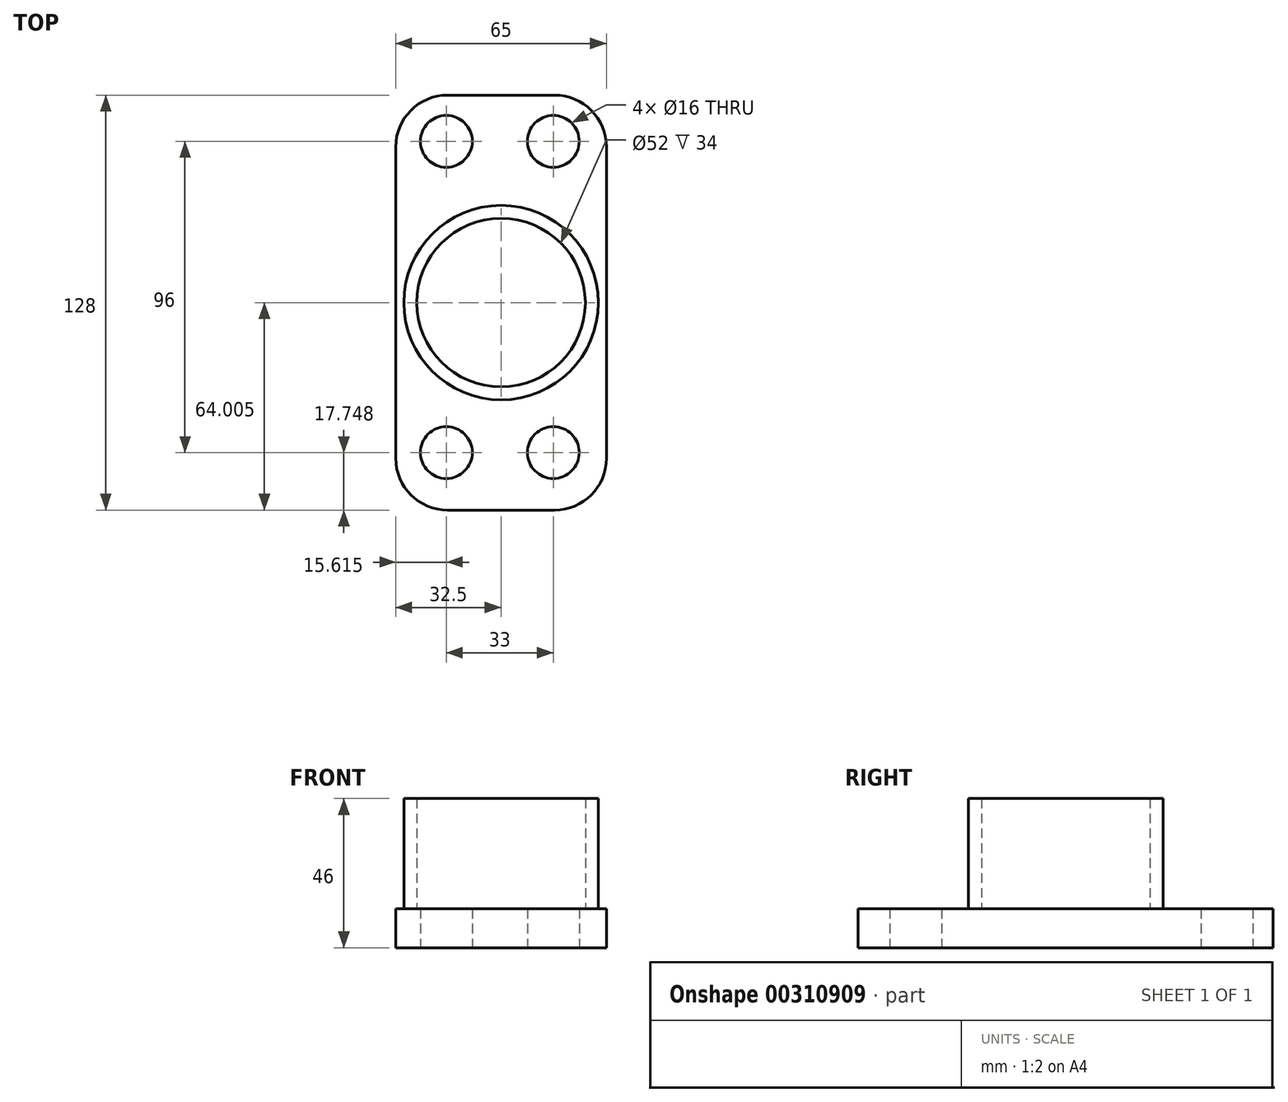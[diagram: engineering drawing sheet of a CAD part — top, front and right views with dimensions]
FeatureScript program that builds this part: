
annotation { "Feature Type Name" : "Feature", "Feature Type Description" : "" }
export const myFeature = defineFeature(function(context is Context, id is Id, definition is map)
    precondition{}
    {
        {
            var Q0;
            Q0=qCreatedBy(makeId("Top.planeOp"),FACE);
            var sketch = newSketch(context, id + "F0", { "sketchPlane" : qUnion([Q0])});
            skLineSegment(sketch, "E0", {"start": v(30.23, -51.74) * mm, "end": v(30.23, 76.26) * mm});
            skLineSegment(sketch, "E1", {"start": v(30.23, 76.26) * mm, "end": v(-34.77, 76.26) * mm});
            skLineSegment(sketch, "E2", {"start": v(-34.77, 76.26) * mm, "end": v(-34.77, -51.74) * mm});
            skLineSegment(sketch, "E3", {"start": v(-34.77, -51.74) * mm, "end": v(30.23, -51.74) * mm});
            skCircle(sketch, "E4", {"center": v(-19.16, 62) * mm, "radius": 8 * mm});
            skCircle(sketch, "E5", {"center": v(13.84, 62) * mm, "radius": 8 * mm});
            skCircle(sketch, "E6", {"center": v(-19.16, -34) * mm, "radius": 8 * mm});
            skCircle(sketch, "E7", {"center": v(13.84, -34) * mm, "radius": 8 * mm});
            skSolve(sketch);
        }
        {
            var Q0;
            Q0=makeQuery(id+"F0.imprint","IMPRINT",FACE,{"disambiguationData":[TD([[makeQuery(id+"F0.imprint","IMPRINT",EDGE,{"derivedFrom":sQuery(id+"F0.wireOp",EDGE,"E0")}),1.0]])]});
            extrude(context, id + "F1", {"entities" : qUnion([Q0]), "depth" : 12 * mm});
        }
        {
            var Q0;
            Q0=makeQuery(id+"F1.opExtrude","SWEPT_EDGE",EDGE,{"disambiguationData":[OSD([sQuery(id+"F0.wireOp",EDGE,"E0"),sQuery(id+"F0.wireOp",EDGE,"E3")])]});
            var Q1;
            Q1=makeQuery(id+"F1.opExtrude","SWEPT_EDGE",EDGE,{"disambiguationData":[OSD([sQuery(id+"F0.wireOp",EDGE,"E2"),sQuery(id+"F0.wireOp",EDGE,"E3")])]});
            var Q2;
            Q2=makeQuery(id+"F1.opExtrude","SWEPT_EDGE",EDGE,{"disambiguationData":[OSD([sQuery(id+"F0.wireOp",EDGE,"E1"),sQuery(id+"F0.wireOp",EDGE,"E2")])]});
            var Q3;
            Q3=makeQuery(id+"F1.opExtrude","SWEPT_EDGE",EDGE,{"disambiguationData":[OSD([sQuery(id+"F0.wireOp",EDGE,"E0"),sQuery(id+"F0.wireOp",EDGE,"E1")])]});
            fillet(context, id + "F2", {"entities" : qUnion([Q0, Q1, Q2, Q3]), "radius" : 16 * mm, "tangentPropagation" : true, "allowEdgeOverflow" : false});
        }
        {
            var Q0;
            Q0=qCreatedBy(makeId("Top.planeOp"),FACE);
            var sketch = newSketch(context, id + "F3", { "sketchPlane" : qUnion([Q0])});
            skCircle(sketch, "E8", {"center": v(-2.27, 12.26) * mm, "radius": 26 * mm});
            skCircle(sketch, "E9", {"center": v(-2.27, 12.26) * mm, "radius": 15 * mm});
            skCircle(sketch, "E10", {"center": v(-2.27, 12.26) * mm, "radius": 10 * mm});
            skLineSegment(sketch, "E11.0", {"start": v(-34.77, 60.26) * mm, "end": v(-34.77, -35.74) * mm});
            skLineSegment(sketch, "E12.0", {"start": v(30.23, -35.74) * mm, "end": v(30.23, 60.26) * mm});
            skLineSegment(sketch, "E13.0", {"start": v(14.23, 76.26) * mm, "end": v(-18.77, 76.26) * mm});
            skLineSegment(sketch, "E14.0", {"start": v(-18.77, -51.74) * mm, "end": v(14.23, -51.74) * mm});
            skLineSegment(sketch, "E15", {"start": v(-2.27, 76.26) * mm, "end": v(-2.27, -51.74) * mm, "construction": true});
            skLineSegment(sketch, "E16", {"start": v(-34.77, 12.26) * mm, "end": v(30.23, 12.26) * mm, "construction": true});
            skCircle(sketch, "E17", {"center": v(-2.27, 12.26) * mm, "radius": 30 * mm});
            skSolve(sketch);
        }
        {
            var Q0;
            Q0 = qSketchRegion(id + "F3", true);
            extrude(context, id + "F4", {"entities" : qUnion([Q0]), "operationType" : NewBodyOperationType.ADD, "depth" : 46 * mm});
        }
    });
